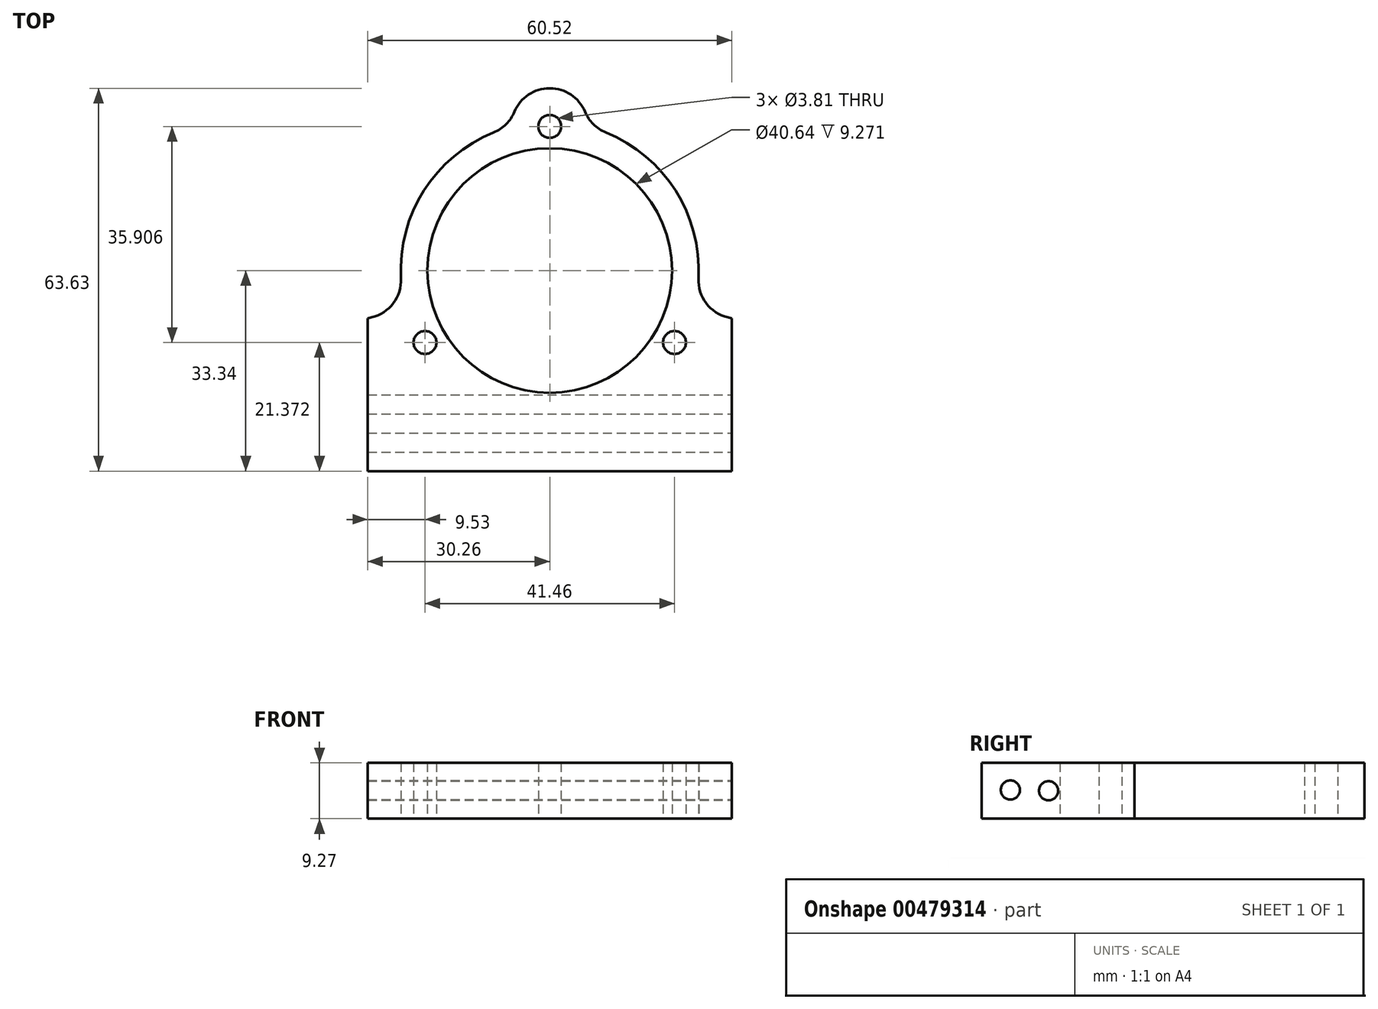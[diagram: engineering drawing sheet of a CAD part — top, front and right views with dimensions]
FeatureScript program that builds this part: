
annotation { "Feature Type Name" : "Feature", "Feature Type Description" : "" }
export const myFeature = defineFeature(function(context is Context, id is Id, definition is map)
    precondition{}
    {
        {
            var Q0;
            Q0=qCreatedBy(makeId("Top.planeOp"),FACE);
            var sketch = newSketch(context, id + "F0", { "sketchPlane" : qUnion([Q0])});
            skCircle(sketch, "E0", {"center": v(0, 0) * mm, "radius": 20.32 * mm});
            skCircle(sketch, "E1", {"center": v(0, 0) * mm, "radius": 24.77 * mm});
            skLineSegment(sketch, "E2", {"start": v(0, 0) * mm, "end": v(0, 42.77) * mm, "construction": true});
            skLineSegment(sketch, "E3", {"start": v(0, 0) * mm, "end": v(-43.71, -25.24) * mm, "construction": true});
            skLineSegment(sketch, "E4", {"start": v(0, 0) * mm, "end": v(46.9, -27.08) * mm, "construction": true});
            skLineSegment(sketch, "E5", {"start": v(-11.23, 0.85) * mm, "end": v(-48.99, -20.95) * mm, "construction": true});
            skLineSegment(sketch, "E6.MirrorCS", {"start": v(-4.88, -10.15) * mm, "end": v(-42.64, -31.95) * mm, "construction": true});
            skLineSegment(sketch, "E7", {"start": v(0.14, -7.41) * mm, "end": v(38.48, -29.55) * mm, "construction": true});
            skLineSegment(sketch, "E8.MirrorCS", {"start": v(6.49, 3.59) * mm, "end": v(44.83, -18.55) * mm, "construction": true});
            skArc(sketch, "E9", {"start": v(-23.9, -6.47) * mm, "mid": v(-26.23, -15.14) * mm, "end": v(-17.56, -17.47) * mm});
            skArc(sketch, "E10", {"start": v(17.56, -17.47) * mm, "mid": v(26.23, -15.14) * mm, "end": v(23.9, -6.47) * mm});
            skCircle(sketch, "E11", {"center": v(0, 23.94) * mm, "radius": 1.9 * mm});
            skCircle(sketch, "E12", {"center": v(-20.73, -11.97) * mm, "radius": 1.9 * mm});
            skCircle(sketch, "E13", {"center": v(20.73, -11.97) * mm, "radius": 1.9 * mm});
            skLineSegment(sketch, "E14", {"start": v(-30.26, -7.94) * mm, "end": v(-30.26, -33.34) * mm});
            skLineSegment(sketch, "E15.MirrorCS", {"start": v(30.26, -7.94) * mm, "end": v(30.26, -33.34) * mm});
            skLineSegment(sketch, "E16", {"start": v(-30.26, -33.34) * mm, "end": v(30.26, -33.34) * mm});
            skLineSegment(sketch, "E17", {"start": v(-6.35, 11.77) * mm, "end": v(-6.35, 67.16) * mm, "construction": true});
            skLineSegment(sketch, "E18.MirrorCS", {"start": v(6.35, 11.77) * mm, "end": v(6.35, 67.16) * mm, "construction": true});
            skArc(sketch, "E19", {"start": v(6.35, 23.94) * mm, "mid": v(0, 30.29) * mm, "end": v(-6.35, 23.94) * mm});
            skLineSegment(sketch, "E20", {"start": v(-30.26, -7.94) * mm, "end": v(-23.9, -6.47) * mm});
            skLineSegment(sketch, "E21", {"start": v(30.26, -7.94) * mm, "end": v(23.9, -6.47) * mm});
            skSolve(sketch);
        }
        {
            var Q0;
            Q0=makeQuery(id+"F0.imprint","IMPRINT",FACE,{"disambiguationData":[TD([[makeQuery(id+"F0.imprint","IMPRINT",EDGE,{"derivedFrom":sQuery(id+"F0.wireOp",EDGE,"E0")}),-1.0]])]});
            var Q1;
            {var subQ0=sQuery(id+"F0.wireOp",EDGE,"E9");Q1=makeQuery(id+"F0.imprint","IMPRINT",FACE,{"disambiguationData":[TD([[makeQuery(id+"F0.imprint","IMPRINT",EDGE,{"derivedFrom":subQ0}),1.0]])]});}
            var Q2;
            {var subQ0=sQuery(id+"F0.wireOp",EDGE,"pi8Cm9jP-h32O-VZzR-VnBJ-4NPhomStRVTA");Q2=makeQuery(id+"F0.imprint","IMPRINT",FACE,{"disambiguationData":[TD([[makeQuery(id+"F0.imprint","IMPRINT",EDGE,{"derivedFrom":subQ0}),1.0]])]});}
            var Q3;
            {var subQ0=sQuery(id+"F0.wireOp",EDGE,"E10");Q3=makeQuery(id+"F0.imprint","IMPRINT",FACE,{"disambiguationData":[TD([[makeQuery(id+"F0.imprint","IMPRINT",EDGE,{"derivedFrom":subQ0}),1.0]])]});}
            var Q4;
            {var subQ0=sQuery(id+"F0.wireOp",EDGE,"P7D2sPVQ-bIUO-sKEJ-Hvsu-Ucmak8lXslGz");Q4=makeQuery(id+"F0.imprint","IMPRINT",FACE,{"disambiguationData":[TD([[makeQuery(id+"F0.imprint","IMPRINT",EDGE,{"derivedFrom":subQ0}),1.0]])]});}
            var Q5;
            {var subQ1=sQuery(id+"F0.wireOp",EDGE,"ZrIFa845-A5xk-iC54-SbUT-vzmD87mmmZLw");Q5=makeQuery(id+"F0.imprint","IMPRINT",FACE,{"disambiguationData":[TD([[makeQuery(id+"F0.imprint","IMPRINT",EDGE,{"derivedFrom":subQ1}),1.0]])]});}
            var Q6;
            {var subQ1=sQuery(id+"F0.wireOp",EDGE,"74ZDynrD-kUol-orQp-wIPQ-E0AyNWxzdnD8");Q6=makeQuery(id+"F0.imprint","IMPRINT",FACE,{"disambiguationData":[TD([[makeQuery(id+"F0.imprint","IMPRINT",EDGE,{"derivedFrom":subQ1}),-1.0]])]});}
            var Q7;
            {var subQ0=sQuery(id+"F0.wireOp",EDGE,"SgoTPPhY-znwD-kxNm-kET9-2jDkmJ3fZYmJ");Q7=makeQuery(id+"F0.imprint","IMPRINT",FACE,{"disambiguationData":[TD([[makeQuery(id+"F0.imprint","IMPRINT",EDGE,{"derivedFrom":subQ0}),1.0]])]});}
            var Q8;
            Q8=makeQuery(id+"F0.imprint","IMPRINT",FACE,{"disambiguationData":[TD([[makeQuery(id+"F0.imprint","IMPRINT",EDGE,{"derivedFrom":sQuery(id+"F0.wireOp",EDGE,"54813680-eaab-4df3-8d17-e395092f1c5b0.MirrorCS")}),-1.0]])]});
            var Q9;
            Q9=makeQuery(id+"F0.imprint","IMPRINT",FACE,{"disambiguationData":[TD([[makeQuery(id+"F0.imprint","IMPRINT",EDGE,{"derivedFrom":sQuery(id+"F0.wireOp",EDGE,"E14")}),1.0]])]});
            var Q10;
            {var subQ4=sQuery(id+"F0.wireOp",EDGE,"JNHPmxil-skpb-Nxat-FCgC-TdduXypQZRyv");Q10=makeQuery(id+"F0.imprint","IMPRINT",FACE,{"disambiguationData":[TD([[makeQuery(id+"F0.imprint","IMPRINT",EDGE,{"derivedFrom":subQ4}),-1.0]])]});}
            var Q11;
            {var subQ0=sQuery(id+"F0.wireOp",EDGE,"E19");Q11=makeQuery(id+"F0.imprint","IMPRINT",FACE,{"disambiguationData":[TD([[makeQuery(id+"F0.imprint","IMPRINT",EDGE,{"derivedFrom":subQ0}),1.0]])]});}
            extrude(context, id + "F1", {"entities" : qUnion([Q0, Q1, Q2, Q3, Q4, Q5, Q6, Q7, Q8, Q9, Q10, Q11]), "depth" : 9.27 * mm});
        }
        {
            var Q0;
            Q0=makeQuery(id+"F1.opExtrude","SWEPT_FACE",FACE,{"disambiguationData":[OSD([sQuery(id+"F0.wireOp",EDGE,"E15.MirrorCS")])]});
            var sketch = newSketch(context, id + "F2", { "sketchPlane" : qUnion([Q0])});
            skCircle(sketch, "E22", {"center": v(-28.58, 4.76) * mm, "radius": 1.59 * mm});
            skCircle(sketch, "E23", {"center": v(-22.23, 4.64) * mm, "radius": 1.59 * mm});
            skPoint(sketch, "E23.centerSnap0", {"position": v(-33.34, 4.64) * mm});
            skSolve(sketch);
        }
        {
            var Q0;
            Q0=makeQuery(id+"F2.imprint","IMPRINT",FACE,{"disambiguationData":[TD([[makeQuery(id+"F2.imprint","IMPRINT",EDGE,{"derivedFrom":sQuery(id+"F2.wireOp",EDGE,"E22")}),1.0]])]});
            var Q1;
            Q1=makeQuery(id+"F2.imprint","IMPRINT",FACE,{"disambiguationData":[TD([[makeQuery(id+"F2.imprint","IMPRINT",EDGE,{"derivedFrom":sQuery(id+"F2.wireOp",EDGE,"E23")}),1.0]])]});
            extrude(context, id + "F3", {"entities" : qUnion([Q0, Q1]), "operationType" : NewBodyOperationType.REMOVE, "endBound" : BoundingType.THROUGH_ALL, "oppositeDirection" : true, "depth" : 25.4 * mm});
        }
        {
            var Q0;
            {var subQ0=sQuery(id+"F0.wireOp",EDGE,"pi8Cm9jP-h32O-VZzR-VnBJ-4NPhomStRVTA");var subQ1=sQuery(id+"F0.wireOp",EDGE,"E1");Q0=makeQuery(id+"F1.opExtrude","SWEPT_EDGE",EDGE,{"disambiguationData":[OSD([subQ1,subQ0]),TDD([makeQuery(id+"F0.imprint","INTERSECT",VERTEX,{"disambiguationData":[OD(1.0)],"derivedFrom":[subQ1,subQ0]})])]});}
            var Q1;
            Q1=makeQuery(id+"F1.opExtrude","SWEPT_EDGE",EDGE,{"disambiguationData":[OSD([sQuery(id+"F0.wireOp",EDGE,"E1"),sQuery(id+"F0.wireOp",EDGE,"E9")])]});
            var Q2;
            Q2=makeQuery(id+"F1.opExtrude","SWEPT_EDGE",EDGE,{"disambiguationData":[OSD([sQuery(id+"F0.wireOp",EDGE,"E1"),sQuery(id+"F0.wireOp",EDGE,"E10")])]});
            var Q3;
            {var subQ0=sQuery(id+"F0.wireOp",EDGE,"pi8Cm9jP-h32O-VZzR-VnBJ-4NPhomStRVTA");var subQ1=sQuery(id+"F0.wireOp",EDGE,"E1");Q3=makeQuery(id+"F1.opExtrude","SWEPT_EDGE",EDGE,{"disambiguationData":[OSD([subQ1,subQ0]),TDD([makeQuery(id+"F0.imprint","INTERSECT",VERTEX,{"disambiguationData":[OD(0.0)],"derivedFrom":[subQ1,subQ0]})])]});}
            var Q4;
            Q4=makeQuery(id+"F1.opExtrude","SWEPT_EDGE",EDGE,{"disambiguationData":[OSD([sQuery(id+"F0.wireOp",EDGE,"E9"),sQuery(id+"F0.wireOp",EDGE,"aA9Hfuaj-3N0G-9vna-cERh-Yd0qJTWrdBFO")])]});
            var Q5;
            Q5=makeQuery(id+"F1.opExtrude","SWEPT_EDGE",EDGE,{"disambiguationData":[OSD([sQuery(id+"F0.wireOp",EDGE,"E10"),sQuery(id+"F0.wireOp",EDGE,"CztHf9pi-abEH-5zDg-esSa-34DTWoixQtr1")])]});
            var Q6;
            {var subQ0=sQuery(id+"F0.wireOp",EDGE,"E19");var subQ1=sQuery(id+"F0.wireOp",EDGE,"E1");Q6=makeQuery(id+"F1.opExtrude","SWEPT_EDGE",EDGE,{"disambiguationData":[OSD([subQ1,subQ0]),TDD([makeQuery(id+"F0.imprint","INTERSECT",VERTEX,{"disambiguationData":[OD(0.0)],"derivedFrom":[subQ1,subQ0]})])]});}
            var Q7;
            {var subQ0=sQuery(id+"F0.wireOp",EDGE,"E19");var subQ1=sQuery(id+"F0.wireOp",EDGE,"E1");Q7=makeQuery(id+"F1.opExtrude","SWEPT_EDGE",EDGE,{"disambiguationData":[OSD([subQ1,subQ0]),TDD([makeQuery(id+"F0.imprint","INTERSECT",VERTEX,{"disambiguationData":[OD(1.0)],"derivedFrom":[subQ1,subQ0]})])]});}
            fillet(context, id + "F4", {"entities" : qUnion([Q0, Q1, Q2, Q3, Q4, Q5, Q6, Q7]), "radius" : 6.35 * mm, "tangentPropagation" : true, "allowEdgeOverflow" : false});
        }
    });
